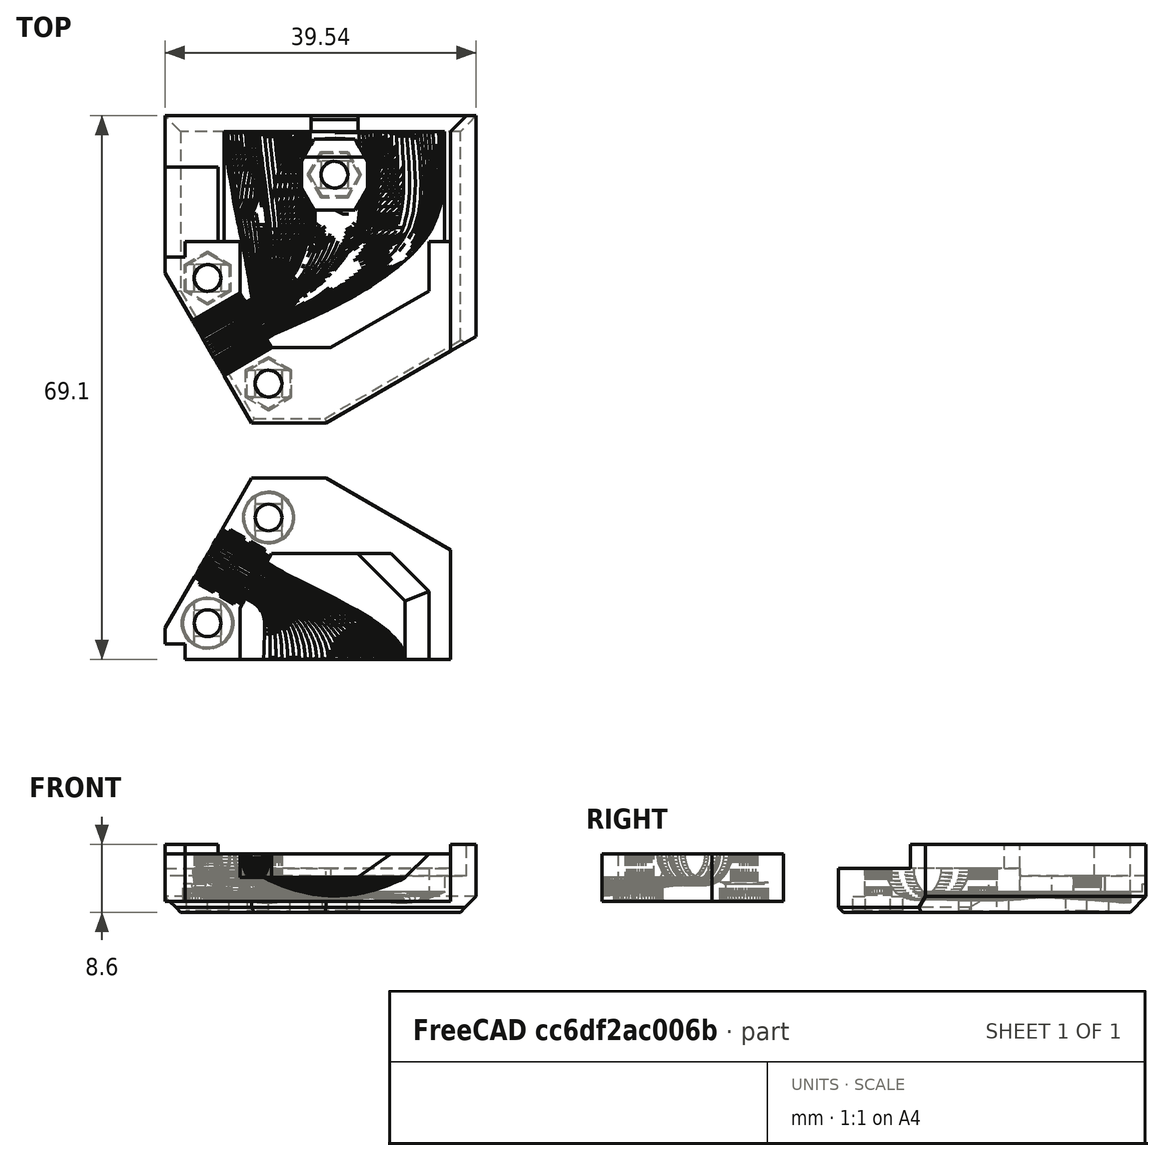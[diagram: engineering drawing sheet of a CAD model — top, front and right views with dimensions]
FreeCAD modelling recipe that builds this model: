
FCSTD DOCUMENT  (FreeCAD 0.18R16146 (Git))
Label: mini-bed-cable-mounter
License: All rights reserved
LicenseURL: http://en.wikipedia.org/wiki/All_rights_reserved
objects: Part::Feature×4, Part::Box×2, Part::Cut×1, Part::MultiFuse×1
note: 8 computed .brp shape members not serialized (recipe doc carries the construction recipe); baked Part::Feature solids carry a one-line shape summary decoded from their .brp

FEATURE [Part::Feature] Top001
  shape: bbox 39.54 x 39.05 x 8.6 mm, 5096 faces, 0 solids (baked)
FEATURE [Part::Feature] Bottom001
  shape: bbox 36.29 x 23.05 x 6 mm, 3262 faces, 0 solids (baked)
FEATURE [Part::Feature] Part__Mirroring001  label="Cut (Mirror #1)001"
  Placement = pos=(0,0,0) rot=(0,1,0;3.14159rad)
  shape: bbox 39.54 x 39.05 x 8.6 mm, 4569 faces (baked)
FEATURE [Part::Feature] Part__Mirroring002  label="Bottom002 (Solid) (Mirror #1)001"
  Placement = pos=(0,0,0) rot=(0,-1,0;3.14159rad)
  shape: bbox 36.29 x 23.05 x 6 mm, 2673 faces (baked)
FEATURE [Part::Box] Box  label="Cube"
  AttacherType = Attacher::AttachEngine3D
  Height = 1
  Length = 10
  Placement = pos=(-5,38.55,2.6) rot=(0,0,1;0rad)
  Width = 0.5
FEATURE [Part::Box] Box001  label="Cube001"
  AttacherType = Attacher::AttachEngine3D
  Height = 10
  Length = 10
  Placement = pos=(-5,33.8,2.6) rot=(0,0,1;0rad)
  Width = 3
FEATURE [Part::Cut] Cut
  Base = -> Part__Mirroring001
  Tool = -> Box001
FEATURE [Part::MultiFuse] Fusion
  Shapes = -> [Box,Cut]
